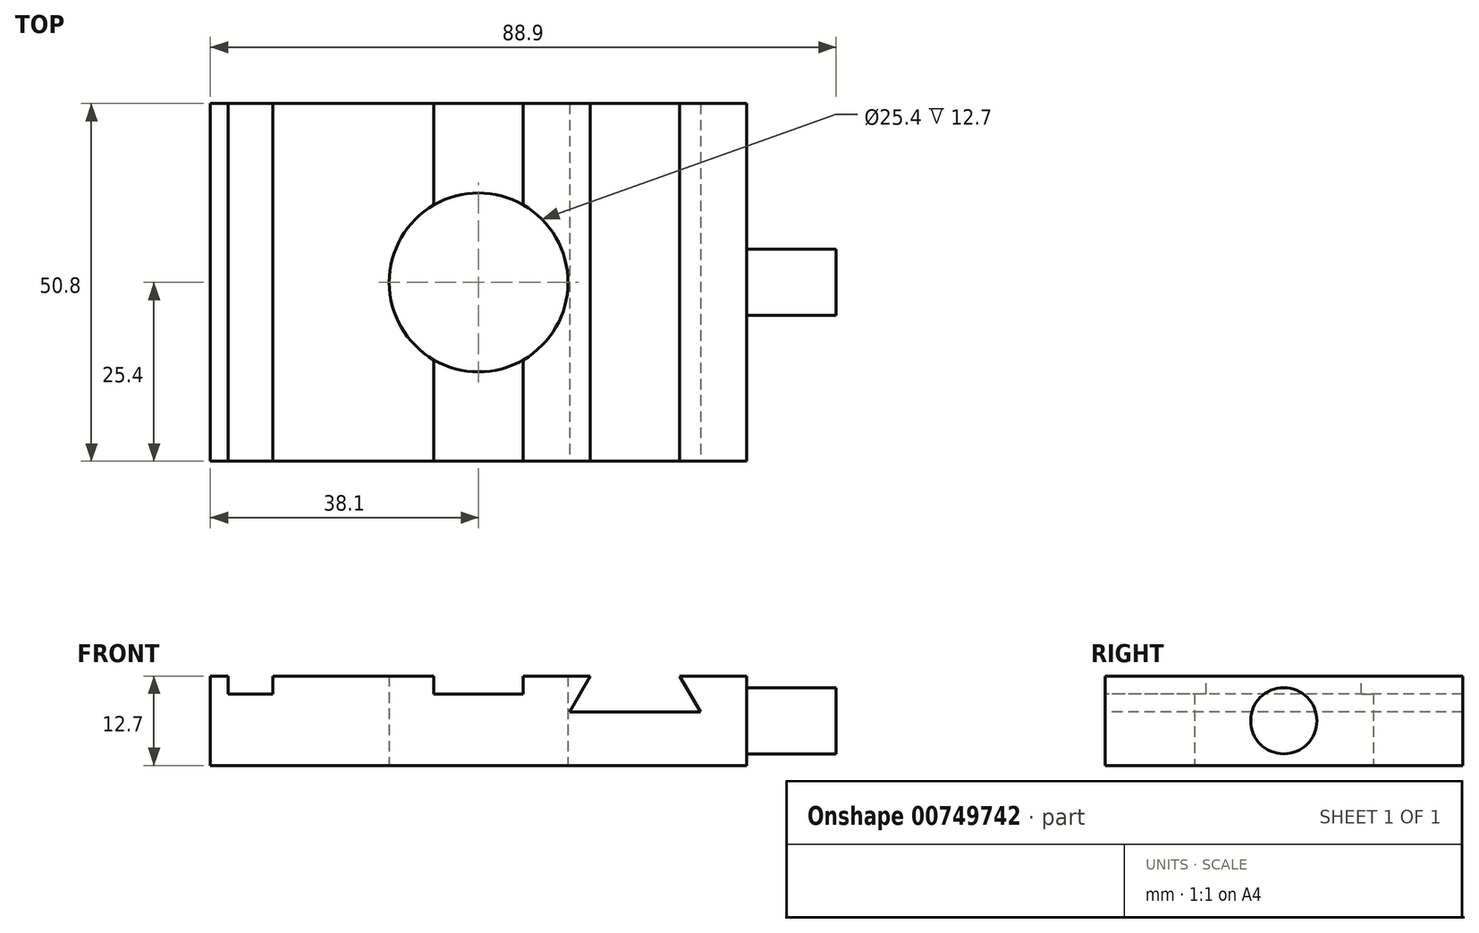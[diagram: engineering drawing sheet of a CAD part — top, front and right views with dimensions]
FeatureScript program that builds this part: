
annotation { "Feature Type Name" : "Feature", "Feature Type Description" : "" }
export const myFeature = defineFeature(function(context is Context, id is Id, definition is map)
    precondition{}
    {
        {
            var Q0;
            Q0=qCreatedBy(makeId("Top.planeOp"),FACE);
            var sketch = newSketch(context, id + "F0", { "sketchPlane" : qUnion([Q0])});
            skLineSegment(sketch, "E0.bottom", {"start": v(38.1, -25.4) * mm, "end": v(-38.1, -25.4) * mm});
            skLineSegment(sketch, "E0.top", {"start": v(38.1, 25.4) * mm, "end": v(-38.1, 25.4) * mm});
            skLineSegment(sketch, "E0.left", {"start": v(38.1, -25.4) * mm, "end": v(38.1, 25.4) * mm});
            skLineSegment(sketch, "E0.right", {"start": v(-38.1, -25.4) * mm, "end": v(-38.1, 25.4) * mm});
            skPoint(sketch, "E0.middle", {"position": v(0, 0) * mm});
            skCircle(sketch, "E1", {"center": v(0, 0) * mm, "radius": 12.7 * mm});
            skSolve(sketch);
        }
        {
            var Q0;
            Q0=makeQuery(id+"F0.imprint","IMPRINT",FACE,{"disambiguationData":[TD([[makeQuery(id+"F0.imprint","IMPRINT",EDGE,{"derivedFrom":sQuery(id+"F0.wireOp",EDGE,"E0.bottom")}),-1.0]])]});
            extrude(context, id + "F1", {"entities" : qUnion([Q0]), "depth" : 12.7 * mm, "offsetDistance" : 25.4 * mm});
        }
        {
            var Q0;
            Q0=makeQuery(id+"F1.opExtrude","CAP_FACE",FACE,{"disambiguationData":[OSD([sQuery(id+"F0.wireOp",EDGE,"E0.bottom"),sQuery(id+"F0.wireOp",EDGE,"E0.top"),sQuery(id+"F0.wireOp",EDGE,"E0.left"),sQuery(id+"F0.wireOp",EDGE,"E0.right"),sQuery(id+"F0.wireOp",EDGE,"E1")])],"isStart":false});
            var sketch = newSketch(context, id + "F2", { "sketchPlane" : qUnion([Q0])});
            skLineSegment(sketch, "E2.bottom", {"start": v(-35.56, 25.4) * mm, "end": v(-29.2, 25.4) * mm});
            skLineSegment(sketch, "E2.top", {"start": v(-35.56, -25.4) * mm, "end": v(-29.2, -25.4) * mm});
            skLineSegment(sketch, "E2.left", {"start": v(-35.56, 25.4) * mm, "end": v(-35.56, -25.4) * mm});
            skLineSegment(sketch, "E2.right", {"start": v(-29.2, 25.4) * mm, "end": v(-29.2, -25.4) * mm});
            skLineSegment(sketch, "E3", {"start": v(-6.35, 25.4) * mm, "end": v(-6.35, -25.4) * mm});
            skLineSegment(sketch, "E4", {"start": v(-6.35, -25.4) * mm, "end": v(6.35, -25.4) * mm});
            skLineSegment(sketch, "E5", {"start": v(6.35, -25.4) * mm, "end": v(6.35, 25.4) * mm});
            skPoint(sketch, "E6", {"position": v(0, 0) * mm});
            skLineSegment(sketch, "E7", {"start": v(-6.35, 25.4) * mm, "end": v(6.35, 25.4) * mm, "construction": true});
            skLineSegment(sketch, "E8", {"start": v(0, 25.4) * mm, "end": v(0, -25.4) * mm, "construction": true});
            skSolve(sketch);
        }
        {
            var Q0;
            Q0 = qSketchRegion(id + "F2", true);
            var Q1;
            {var subQ0=sQuery(id+"F2.wireOp",EDGE,"E4");Q1=makeQuery(id+"F2.imprint","IMPRINT",FACE,{"disambiguationData":[TD([[makeQuery(id+"F2.imprint","IMPRINT",EDGE,{"derivedFrom":subQ0}),-1.0]])]});}
            var Q2;
            {var subQ0=sQuery(id+"F2.wireOp",EDGE,"E3");var subQ1=makeQuery(id+"F1.opExtrude","CAP_EDGE",EDGE,{"disambiguationData":[OSD([sQuery(id+"F0.wireOp",EDGE,"E0.top")])],"isStart":false});var subQ2=makeQuery(id+"F2.imprint","INTERSECT",VERTEX,{"derivedFrom":[subQ1,subQ0]});Q2=makeQuery(id+"F2.imprint","IMPRINT",FACE,{"disambiguationData":[TD([[makeQuery(id+"F2.imprint","IMPRINT",EDGE,{"disambiguationData":[TD([[subQ2,-1.0]])],"derivedFrom":subQ0}),1.0]])]});}
            extrude(context, id + "F3", {"entities" : qUnion([Q0, Q1, Q2]), "operationType" : NewBodyOperationType.REMOVE, "oppositeDirection" : true, "depth" : 2.54 * mm, "offsetDistance" : 25.4 * mm});
        }
        {
            var Q0;
            Q0=makeQuery(id+"F1.opExtrude","SWEPT_FACE",FACE,{"disambiguationData":[OSD([sQuery(id+"F0.wireOp",EDGE,"E0.bottom")])]});
            var sketch = newSketch(context, id + "F4", { "sketchPlane" : qUnion([Q0])});
            skLineSegment(sketch, "E9", {"start": v(15.88, 12.7) * mm, "end": v(12.94, 7.62) * mm});
            skLineSegment(sketch, "E10", {"start": v(12.94, 7.62) * mm, "end": v(31.5, 7.62) * mm});
            skLineSegment(sketch, "E11", {"start": v(31.5, 7.62) * mm, "end": v(28.58, 12.7) * mm});
            skLineSegment(sketch, "E12", {"start": v(22.23, 12.7) * mm, "end": v(22.23, 7.62) * mm, "construction": true});
            skPoint(sketch, "E12.endSnap0", {"position": v(22.23, 7.62) * mm});
            skPoint(sketch, "E13", {"position": v(0, 10.16) * mm});
            skPoint(sketch, "E14", {"position": v(0, 0) * mm});
            skPoint(sketch, "E15", {"position": v(22.23, 12.7) * mm});
            skSolve(sketch);
        }
        {
            var Q0;
            Q0 = qSketchRegion(id + "F4", true);
            var Q1;
            {var subQ0=sQuery(id+"F4.wireOp",EDGE,"E9");Q1=makeQuery(id+"F4.imprint","IMPRINT",FACE,{"disambiguationData":[TD([[makeQuery(id+"F4.imprint","IMPRINT",EDGE,{"derivedFrom":subQ0}),1.0]])]});}
            extrude(context, id + "F5", {"entities" : qUnion([Q0, Q1]), "operationType" : NewBodyOperationType.REMOVE, "endBound" : BoundingType.THROUGH_ALL, "oppositeDirection" : true, "depth" : 25.4 * mm, "offsetDistance" : 25.4 * mm});
        }
        {
            var Q0;
            Q0=makeQuery(id+"F1.opExtrude","SWEPT_FACE",FACE,{"disambiguationData":[OSD([sQuery(id+"F0.wireOp",EDGE,"E0.left")])]});
            var sketch = newSketch(context, id + "F6", { "sketchPlane" : qUnion([Q0])});
            skCircle(sketch, "E16", {"center": v(0, 6.35) * mm, "radius": 4.7 * mm});
            skPoint(sketch, "E16.centerSnap0", {"position": v(-25.4, 6.35) * mm});
            skPoint(sketch, "E16.centerSnap1", {"position": v(0, 12.7) * mm});
            skSolve(sketch);
        }
        {
            var Q0;
            Q0=makeQuery(id+"F6.imprint","IMPRINT",FACE,{"disambiguationData":[TD([[makeQuery(id+"F6.imprint","IMPRINT",EDGE,{"derivedFrom":sQuery(id+"F6.wireOp",EDGE,"E16")}),1.0]])]});
            extrude(context, id + "F7", {"entities" : qUnion([Q0]), "operationType" : NewBodyOperationType.ADD, "depth" : 12.7 * mm, "offsetDistance" : 25.4 * mm});
        }
    });
